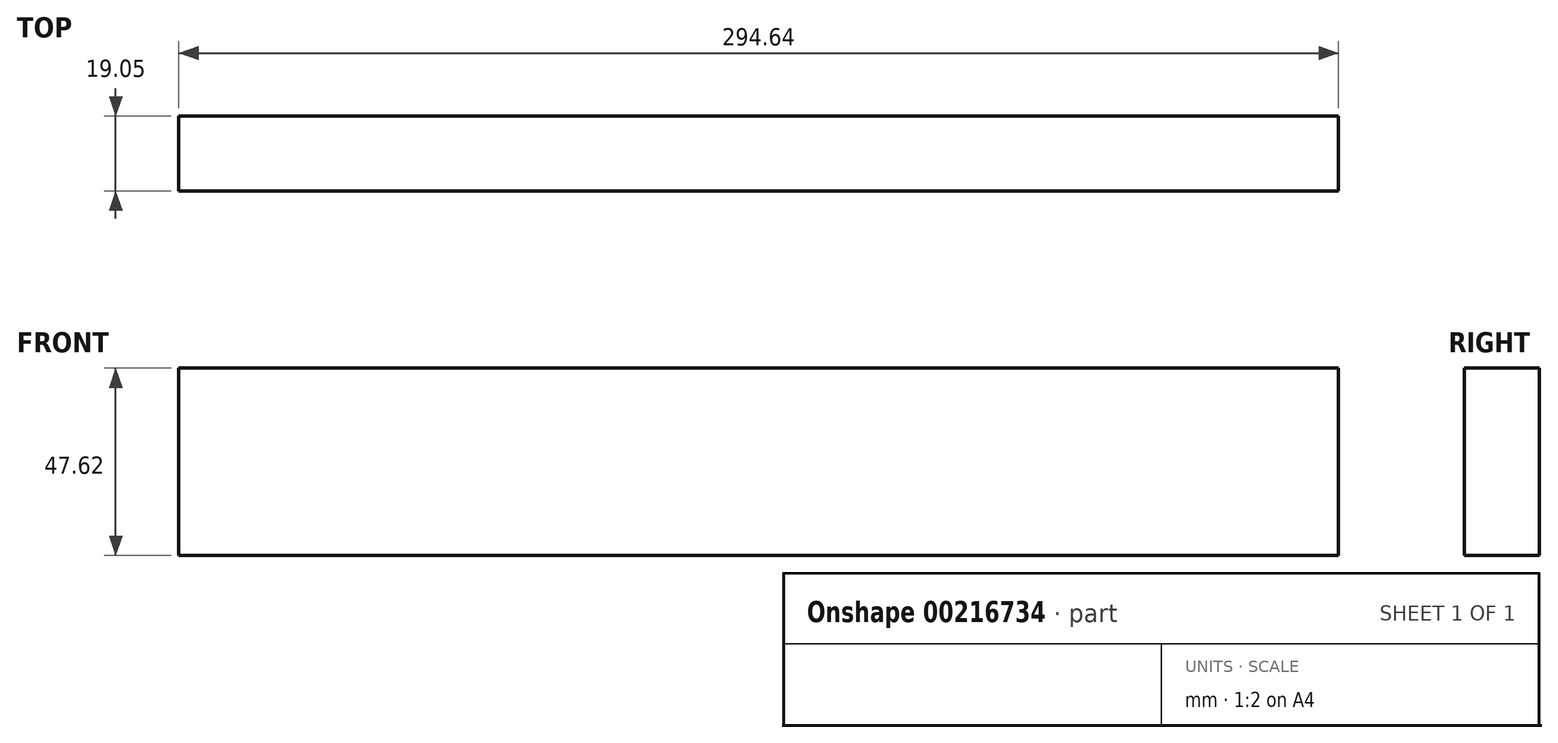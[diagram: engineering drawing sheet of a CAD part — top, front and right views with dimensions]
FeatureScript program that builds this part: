
annotation { "Feature Type Name" : "Feature", "Feature Type Description" : "" }
export const myFeature = defineFeature(function(context is Context, id is Id, definition is map)
    precondition{}
    {
        {
            var Q0;
            Q0=qCreatedBy(makeId("Front.planeOp"),FACE);
            var sketch = newSketch(context, id + "F0", { "sketchPlane" : qUnion([Q0])});
            skLineSegment(sketch, "E0.bottom", {"start": v(4.48, 0) * mm, "end": v(299.12, 0) * mm});
            skLineSegment(sketch, "E0.top", {"start": v(4.48, 47.63) * mm, "end": v(299.12, 47.63) * mm});
            skLineSegment(sketch, "E0.left", {"start": v(4.48, 0) * mm, "end": v(4.48, 47.63) * mm});
            skLineSegment(sketch, "E0.right", {"start": v(299.12, 0) * mm, "end": v(299.12, 47.62) * mm});
            skSolve(sketch);
        }
        {
            var Q0;
            Q0 = qSketchRegion(id + "F0", true);
            extrude(context, id + "F1", {"entities" : qUnion([Q0]), "depth" : 19.05 * mm});
        }
    });
